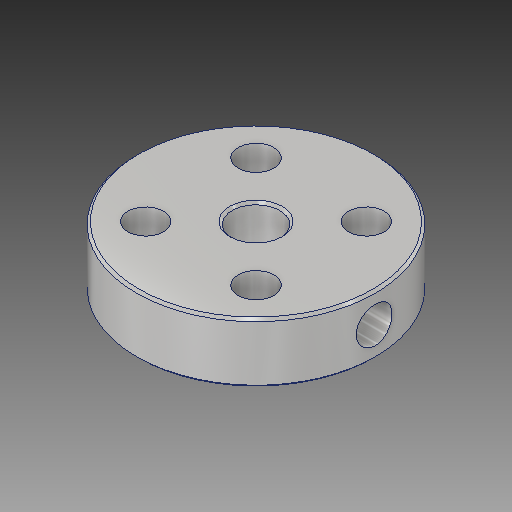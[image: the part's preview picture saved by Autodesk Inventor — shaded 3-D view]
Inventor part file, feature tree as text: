
AUTODESK INVENTOR PART (.ipt)
format: ipt  version: 2019 (Build 230136000, 136)  size: 171,520 bytes
history: mixed  units: in
note: dims shown in document units (in); Inventor stores cm internally (conversion verified against a paired STEP export)
features: other x2, chamfer x1, imported_body x1
ambient origin geometry x8: Origin, YZ Plane, XZ Plane, XY Plane, X Axis, Y Axis, Z Axis, Center Point
bodies: Solid1 (imported_parasolid)
feature tree (4):
  other  "aluminium-nut-1.SLDPRT"
  chamfer  "Chamfer1"  Distance=0.0079in Angle=45.0deg
  other  "Вырез-Вытянуть4"
  imported_body  NMx_Import_Brep_tag  [imported B-rep: ~7 faces, bbox_mm=[0.0, 0.0, 0.0]]
